# Revit family: Barrisol GTS 375-17
name_source: partatom
category: Modèles génériques
revit_build: Autodesk Revit 2018 (Build: 20170223_1515(x64)
units: mm (PartAtom-declared; Revit-internal decimal feet)

## family parameters
Cote de connecteur circulaire = Utiliser le diamètre
Couper avec des vides une fois chargée = Non
Hôte = Face
Partagée = Non
Peut héberger une armature = Non
Point de calcul de pièce = Non
Type d'élément = Normal

## types (1)
- BGTMS 375/17
    Barrisol GTS = BGTMS 375/17
    Capot (BGTMS 375/19) = Aluminium
    Commentaires du type = BGTMS 375/17 = BGTMS 375/18 + BGTMS 375/19
    Description = GTS by Barrisol
    Elévation par défaut = 0 mm  [stored 0 ft]
    Fabricant = Barrisol
    LED = LED
    Membrane 1 = Textile de verre
    Membrane 2 = Toile transparente
    Modèle = Barrisol BGTMS 375/17
    Note d'identification = BGTMS 375/17
    Rail (BGTMS 375/18) = Aluminium
    URL = https://barrisol.com

note: [stored X ft] marks values corroborated as IEEE doubles in the binary element streams (Revit-internal decimal feet)

## geometry (parser evidence)
native form markers: Blend x8
no freeform markers — native parametric forms only
